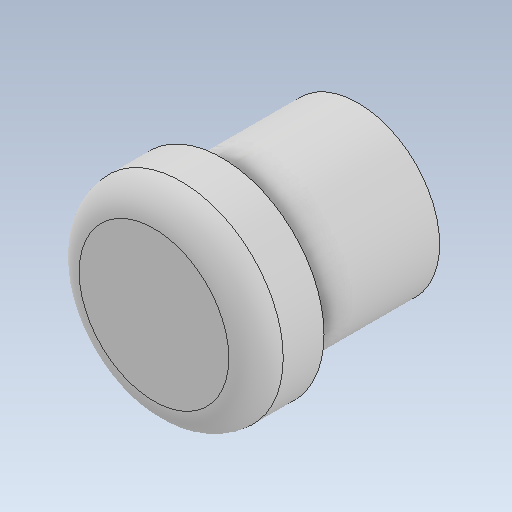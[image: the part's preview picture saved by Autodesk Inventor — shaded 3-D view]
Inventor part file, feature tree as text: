
AUTODESK INVENTOR PART (.ipt)
format: ipt  version: 2020 (Build 240168000, 168)  size: 152,064 bytes
history: native  units: mm
features: sketch x3, extrude x2, fillet x1, hole x1
ambient origin geometry x8: Origin, YZ Plane, XZ Plane, XY Plane, X Axis, Y Axis, Z Axis, Center Point
bodies: Solid1 (feature_tree)
feature tree (7):
  extrude  "Extrusion1"  Depth=12.0mm
  extrude  "Extrusion2"  Depth=15.0mm
  fillet  "Fillet1"  Radius=5.0mm
  hole  "Hole1"  [1 undecoded]
  sketch  "Sketch1"  dims[d0=6.3mm d1=12.0mm]
  sketch  "Sketch2"  dims[d2=10.0mm d3=0.0mm d4=15.0mm d5=5.0mm d6=0.0mm]
  sketch  "Sketch3"  dims[d7=2.0mm d8=5.0mm d9=2.5mm d10=6.0mm d11=10.0mm d12=2.0mm d13=90.0deg d14=8.0mm d15=20.594885mm]
note: 1 required parameter value undecoded (feature->parameter linkage not recoverable at this tier; creation-order binding heuristic only, values carry confidence <= 0.55)
